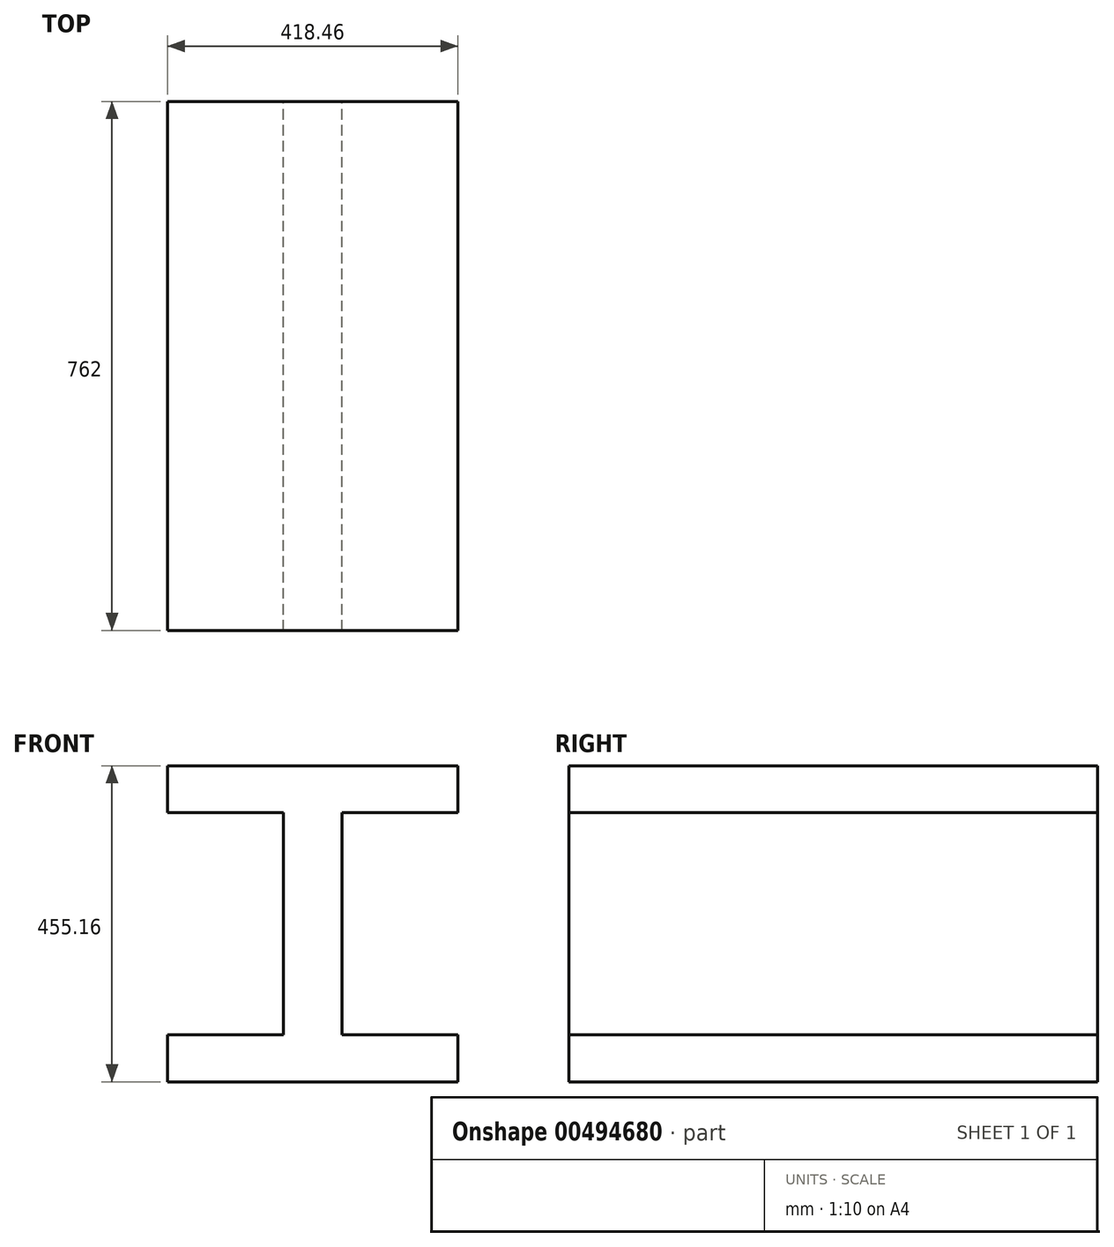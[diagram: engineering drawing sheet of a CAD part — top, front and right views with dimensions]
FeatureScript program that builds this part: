
annotation { "Feature Type Name" : "Feature", "Feature Type Description" : "" }
export const myFeature = defineFeature(function(context is Context, id is Id, definition is map)
    precondition{}
    {
        {
            var Q0;
            Q0=qCreatedBy(makeId("Front.planeOp"),FACE);
            var sketch = newSketch(context, id + "F0", { "sketchPlane" : qUnion([Q0])});
            skLineSegment(sketch, "E0", {"start": v(0, 0) * mm, "end": v(-42.04, 0) * mm});
            skLineSegment(sketch, "E1", {"start": v(-42.04, 0) * mm, "end": v(-42.04, 160.02) * mm});
            skLineSegment(sketch, "E2", {"start": v(-42.04, 160.02) * mm, "end": v(-209.23, 160.02) * mm});
            skLineSegment(sketch, "E3", {"start": v(-209.23, 160.02) * mm, "end": v(-209.23, 227.58) * mm});
            skLineSegment(sketch, "E4", {"start": v(-209.23, 227.58) * mm, "end": v(0, 227.58) * mm});
            skLineSegment(sketch, "E5", {"start": v(0, 0) * mm, "end": v(0, 227.58) * mm, "construction": true});
            skLineSegment(sketch, "E6", {"start": v(0, 0) * mm, "end": v(-209.23, 0) * mm, "construction": true});
            skLineSegment(sketch, "E7.MirrorCS", {"start": v(0, 0) * mm, "end": v(209.23, 0) * mm, "construction": true});
            skLineSegment(sketch, "E8.MirrorCS", {"start": v(42.04, 0) * mm, "end": v(42.04, 160.02) * mm});
            skLineSegment(sketch, "E9.MirrorCS", {"start": v(42.04, 160.02) * mm, "end": v(209.23, 160.02) * mm});
            skLineSegment(sketch, "E10.MirrorCS", {"start": v(209.23, 160.02) * mm, "end": v(209.23, 227.58) * mm});
            skLineSegment(sketch, "E11.MirrorCS", {"start": v(209.23, 227.58) * mm, "end": v(0, 227.58) * mm});
            skLineSegment(sketch, "E12.MirrorCS", {"start": v(42.04, 0) * mm, "end": v(42.04, -160.02) * mm});
            skLineSegment(sketch, "E13.MirrorCS", {"start": v(-42.04, 0) * mm, "end": v(-42.04, -160.02) * mm});
            skLineSegment(sketch, "E14.MirrorCS", {"start": v(0, 0) * mm, "end": v(0, -227.58) * mm, "construction": true});
            skLineSegment(sketch, "E15.MirrorCS", {"start": v(209.23, -227.58) * mm, "end": v(0, -227.58) * mm});
            skLineSegment(sketch, "E16.MirrorCS", {"start": v(42.04, -160.02) * mm, "end": v(209.23, -160.02) * mm});
            skLineSegment(sketch, "E17.MirrorCS", {"start": v(209.23, -160.02) * mm, "end": v(209.23, -227.58) * mm});
            skLineSegment(sketch, "E18.MirrorCS", {"start": v(-209.23, -160.02) * mm, "end": v(-209.23, -227.58) * mm});
            skLineSegment(sketch, "E19.MirrorCS", {"start": v(-42.04, -160.02) * mm, "end": v(-209.23, -160.02) * mm});
            skLineSegment(sketch, "E20.MirrorCS", {"start": v(-209.23, -227.58) * mm, "end": v(0, -227.58) * mm});
            skSolve(sketch);
        }
        {
            var Q0;
            Q0 = qSketchRegion(id + "F0", true);
            extrude(context, id + "F1", {"entities" : qUnion([Q0]), "depth" : 762 * mm});
        }
    });
